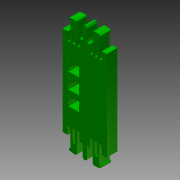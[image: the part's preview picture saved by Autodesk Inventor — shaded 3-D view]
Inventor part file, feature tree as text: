
AUTODESK INVENTOR PART (.ipt)
format: ipt  version: 2012 SP1 (Build 160190100, 190)  size: 247,296 bytes
history: native  units: in
note: dims shown in document units (in); Inventor stores cm internally (conversion verified against a paired STEP export)
features: other x3, extrude x1
ambient origin geometry x8: Origin, YZ Plane, XZ Plane, XY Plane, X Axis, Y Axis, Z Axis, Center Point
bodies: Solid1 (feature_tree)
feature tree (4):
  other  "skeleton.ipt"
  other  "STOCK_12MM"
  extrude  "Extrusion1"  Depth=0.3937in
  other  "THROUGH-CUT"
